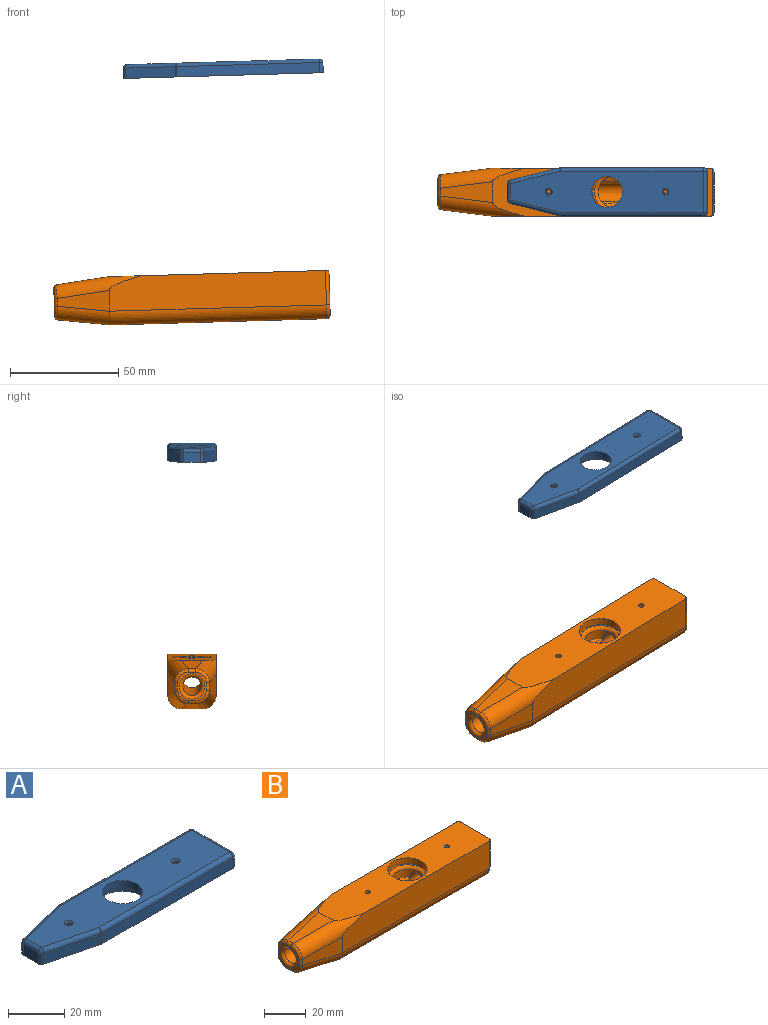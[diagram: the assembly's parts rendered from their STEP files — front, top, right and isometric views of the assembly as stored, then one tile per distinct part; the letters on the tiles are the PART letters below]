
ASSEMBLY  parts=2 mates=1
PART A: 33 faces, bbox 92.1x22.3x6.4 mm
  f0: plane 7.58x4.75mm, normal (-1,0,0), area 36mm2, adj f5,f10,f16,f17
  f1: plane 65.9x4.75mm, normal (0,-1,0), area 313mm2, adj f5,f19,f23,f25
  f2: plane 19.05x4.75mm, normal (1,0,0), area 90.5mm2, adj f5,f13,f18,f19
  f3: plane 65.9x4.75mm, normal (0,1,0), area 313mm2, adj f5,f8,f12,f13
  f4: plane 88.9x19.05mm, normal (0,0,1), area 1385.3mm2, adj f11,f12,f17,f18,f22,f23,f26,f30
  f5: plane 92.1x22.25mm, normal (0,0,-1), area 1607.8mm2, adj f0,f1,f2,f3,f6,f7,f8,f10
  f6: plane 23x5.73mm, normal (-0.24,0.97,0), area 112.6mm2, adj f5,f8,f10,f11
  f7: plane 23x5.73mm, normal (-0.24,-0.97,0), area 112.6mm2, adj f5,f16,f22,f25
  f8: cylinder r=1.6mm len=4.75mm, axis (0,0,-1), area 1.9mm2, adj f3,f5,f6,f9
  f9: sphere r=1.6mm, area 0.6mm2, adj f8,f11,f12
  f10: cylinder r=1.6mm len=4.75mm, axis (0,0,1), area 10.1mm2, adj f0,f5,f6,f14
  f11: cylinder r=1.6mm len=23.38mm, axis (0.97,0.24,0), area 59.6mm2, adj f4,f6,f9,f14
  f12: cylinder r=1.6mm len=65.9mm, axis (1,0,0), area 165.6mm2, adj f3,f4,f9,f15
  f13: cylinder r=1.6mm len=4.75mm, axis (0,0,1), area 11.9mm2, adj f2,f3,f5,f15
  f14: sphere r=1.6mm, area 3.4mm2, adj f10,f11,f17
  f15: sphere r=1.6mm, area 4mm2, adj f12,f13,f18
  f16: cylinder r=1.6mm len=4.75mm, axis (0,0,1), area 10.1mm2, adj f0,f5,f7,f20
  f17: cylinder r=1.6mm len=7.58mm, axis (0,1,0), area 19.1mm2, adj f0,f4,f14,f20
  f18: cylinder r=1.6mm len=19.05mm, axis (0,-1,0), area 47.9mm2, adj f2,f4,f15,f21
  f19: cylinder r=1.6mm len=4.75mm, axis (0,0,-1), area 11.9mm2, adj f1,f2,f5,f21
  f20: sphere r=1.6mm, area 3.4mm2, adj f16,f17,f22
  f21: sphere r=1.6mm, area 4mm2, adj f18,f19,f23
  f22: cylinder r=1.6mm len=23.38mm, axis (0.97,-0.24,0), area 59.6mm2, adj f4,f7,f20,f24
  f23: cylinder r=1.6mm len=65.9mm, axis (-1,0,0), area 165.6mm2, adj f1,f4,f21,f24
  f24: sphere r=1.6mm, area 0.6mm2, adj f22,f23,f25
  f25: cylinder r=1.6mm len=4.75mm, axis (0,0,1), area 1.9mm2, adj f1,f5,f7,f24
  f26: cylinder r=7.15mm len=14.3mm, axis (0,0,-1), area 142.6mm2, adj f4,f27
  f27: plane 19.05x19.05mm, normal (0,0,-1), area 124.4mm2, adj f26,f28
  f28: cylinder r=9.53mm len=19.05mm, axis (0,0,-1), area 190mm2, adj f5,f27
  f29: cylinder r=1mm len=5.76mm, axis (0,0,1), area 36.2mm2, adj f5,f30
  f30: cone r=1mm half-angle=45deg, axis (0,0,1), area 6.8mm2, adj f4,f29
  f31: cylinder r=1mm len=5.76mm, axis (0,0,1), area 36.2mm2, adj f5,f32
  f32: cone r=1mm half-angle=45deg, axis (0,0,1), area 6.8mm2, adj f4,f31
PART B: 46 faces, bbox 134x33x31.7 mm
  f0: cone r=0mm half-angle=59deg, axis (0,0,1), area 0mm2, adj f17,f42
  f1: plane 13.03x13.03mm, normal (-1,0,0), area 41.6mm2, adj f26,f27,f28,f29,f30,f31,f32,f33
  f2: plane 106.9x22.9mm, normal (0,-1,0), area 1554.6mm2, adj f5,f8,f12,f15,f34
  f3: plane 20.65x19.05mm, normal (1,0,0), area 274.6mm2, adj f5,f34,f35,f36,f37,f38,f44
  f4: plane 106.9x22.9mm, normal (0,1,0), area 1554.6mm2, adj f5,f9,f14,f16,f38
  f5: plane 108.5x29.25mm, normal (0,0,1), area 1894.4mm2, adj f2,f3,f4,f10,f15,f16,f19,f22
  f6: plane 99.9x9.55mm, normal (0,0,-1), area 954mm2, adj f7,f12,f14,f36
  f7: plane 24.1x9.65mm, normal (-0.12,0,-0.99), area 160.9mm2, adj f6,f11,f12,f13,f14,f30
  f8: plane 24.1x9.65mm, normal (-0.12,-0.99,0), area 160.9mm2, adj f2,f11,f12,f15,f26
  f9: plane 24.1x9.65mm, normal (-0.12,0.99,0), area 160.9mm2, adj f4,f13,f14,f16,f33
  f10: plane 24.1x9.65mm, normal (-0.12,0,0.99), area 160.9mm2, adj f5,f15,f16,f29
  f11: cylinder r=6.35mm len=24.42mm, axis (0.98,-0.12,-0.12), area 241.7mm2, adj f7,f8,f12,f28
  f12: cylinder r=6.35mm len=100.06mm, axis (1,0,0), area 997.5mm2, adj f2,f6,f7,f8,f11,f35
  f13: cylinder r=6.35mm len=24.42mm, axis (0.98,0.12,-0.12), area 241.7mm2, adj f7,f9,f14,f32
  f14: cylinder r=6.35mm len=100.06mm, axis (-1,0,0), area 997.5mm2, adj f4,f6,f7,f9,f13,f37
  f15: cylinder r=6.35mm len=39.4mm, axis (-0.98,0.12,-0.12), area 316.8mm2, adj f2,f5,f8,f10,f27
  f16: cylinder r=6.35mm len=39.4mm, axis (-0.98,-0.12,-0.12), area 316.8mm2, adj f4,f5,f9,f10,f31
  f17: cylinder r=7.15mm len=14.3mm, axis (0,0,1), area 137.2mm2, adj f0,f20,f39,f40,f41,f42,f45
  f18: plane 19.05x19.05mm, normal (0,0,1), area 44.5mm2, adj f19,f45
  f19: cylinder r=9.53mm len=19.05mm, axis (0,0,1), area 209.5mm2, adj f5,f18
  f20: cone r=0mm half-angle=59deg, axis (0,0,1), area 0mm2, adj f17,f39
  f21: cone r=0mm half-angle=59deg, axis (0,0,1), area 2mm2, adj f22,f25
  f22: cylinder r=1.28mm len=6.75mm, axis (0,0,1), area 54.3mm2, adj f5,f21
  f23: cone r=0mm half-angle=59deg, axis (0,0,1), area 2mm2, adj f24,f25
  f24: cylinder r=1.28mm len=6.75mm, axis (0,0,1), area 54.3mm2, adj f5,f23
  f25: cylinder r=4.29mm len=123.8mm, axis (-1,0,0), area 3120.5mm2, adj f21,f23,f39,f40,f41,f42,f43,f44
  f26: cylinder r=1.6mm len=3.6mm, axis (0,0,1), area 8.3mm2, adj f1,f8,f27,f28
  f27: bspline ~6.3x6.3mm, area 20.1mm2, adj f1,f15,f26,f29
  f28: bspline ~6.3x6.3mm, area 20.1mm2, adj f1,f11,f26,f30
  f29: cylinder r=1.6mm len=3.6mm, axis (0,-1,0), area 8.3mm2, adj f1,f10,f27,f31
  f30: cylinder r=1.6mm len=3.6mm, axis (0,-1,0), area 8.3mm2, adj f1,f7,f28,f32
  f31: bspline ~6.3x6.3mm, area 20.1mm2, adj f1,f16,f29,f33
  f32: bspline ~6.3x6.3mm, area 20.1mm2, adj f1,f13,f30,f33
  f33: cylinder r=1.6mm len=3.6mm, axis (0,0,1), area 8.3mm2, adj f1,f9,f31,f32
  f34: cylinder r=1.6mm len=15.9mm, axis (0,0,-1), area 40mm2, adj f2,f3,f5,f35
  f35: torus R=4.75mm, axis (-1,0,0), area 22.8mm2, adj f3,f12,f34,f36
  f36: cylinder r=1.6mm len=9.55mm, axis (0,1,0), area 24mm2, adj f3,f6,f35,f37
  f37: torus R=4.75mm, axis (-1,0,0), area 22.8mm2, adj f3,f14,f36,f38
  f38: cylinder r=1.6mm len=15.9mm, axis (0,0,1), area 40mm2, adj f3,f4,f5,f37
  f39: bspline ~16.62x3.71mm, area 19mm2, adj f17,f20,f25,f40,f41
  f40: bspline ~9.63x6.22mm, area 26.8mm2, adj f17,f25,f39,f42
  f41: bspline ~9.63x6.22mm, area 26.8mm2, adj f17,f25,f39,f42
  f42: bspline ~16.62x3.71mm, area 19mm2, adj f0,f17,f25,f40,f41
  f43: torus R=5.89mm, axis (-1,0,0), area 77mm2, adj f1,f25
  f44: torus R=5.89mm, axis (-1,0,0), area 77mm2, adj f3,f25
  f45: torus R=8.75mm, axis (0,0,1), area 122.1mm2, adj f17,f18
PLACE A rot(axis=(0,-1,0),1.7deg) t=(6.35,13.6,-13.54)mm
PLACE B rot(axis=(0,-1,0),1.7deg) t=(-7.6,13.6,-119.45)mm
MATE slider B.f0 <-> A.f26  axis (-0.03,0,1) through (9.57,13.6,-107.83)mm
